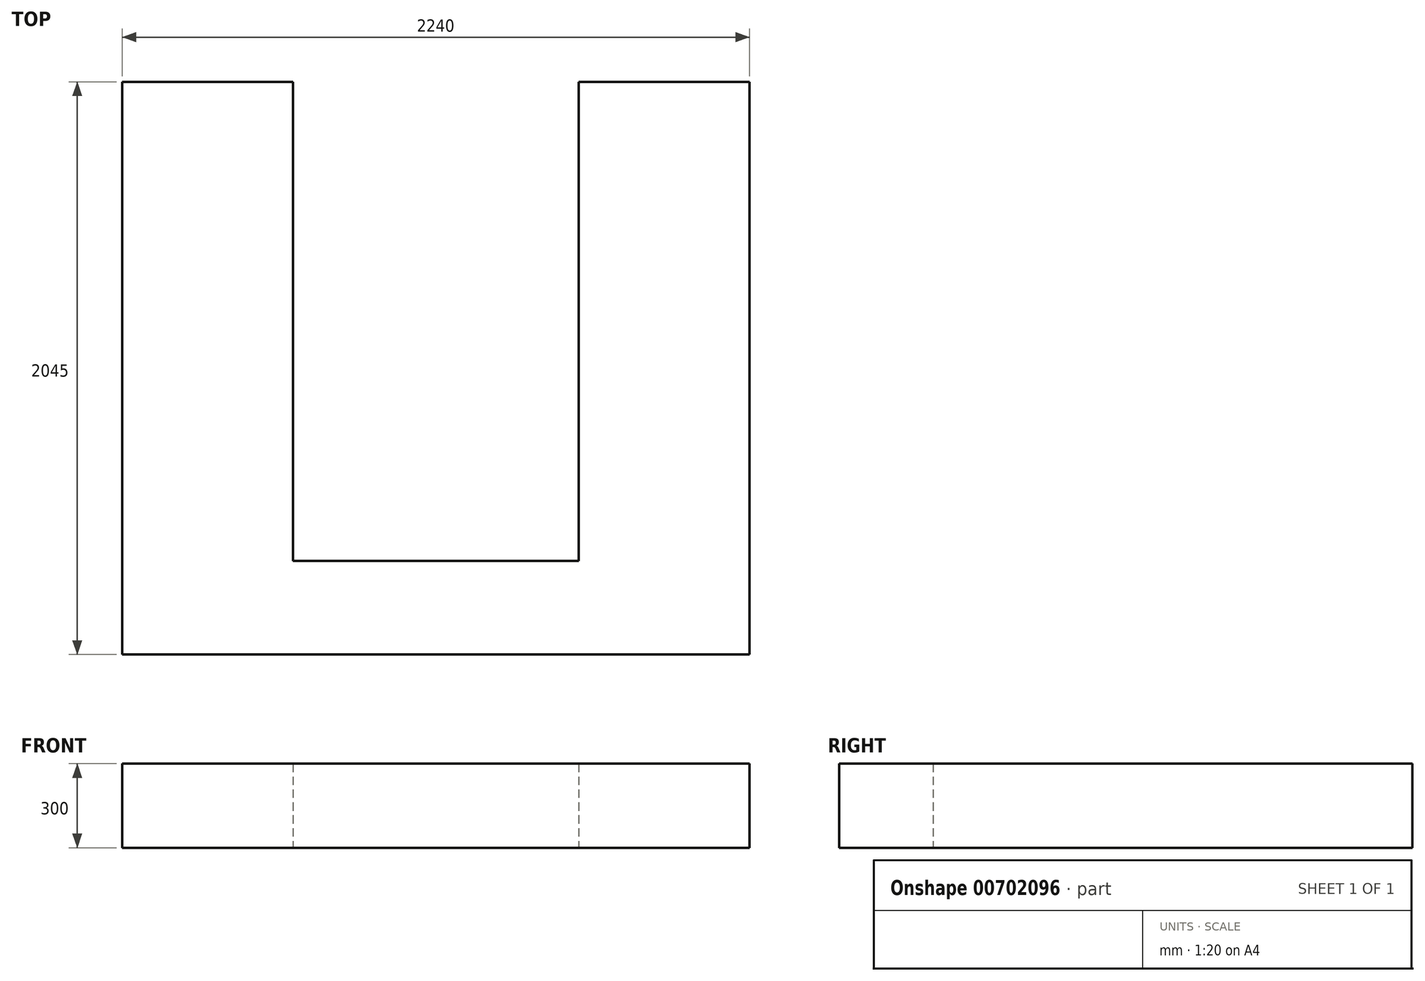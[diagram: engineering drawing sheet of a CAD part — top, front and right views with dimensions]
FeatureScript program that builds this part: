
annotation { "Feature Type Name" : "Feature", "Feature Type Description" : "" }
export const myFeature = defineFeature(function(context is Context, id is Id, definition is map)
    precondition{}
    {
        {
            var Q0;
            Q0=qCreatedBy(makeId("Top.planeOp"),FACE);
            var sketch = newSketch(context, id + "F0", { "sketchPlane" : qUnion([Q0])});
            skLineSegment(sketch, "E0", {"start": v(0, 0) * mm, "end": v(2240, 0) * mm});
            skLineSegment(sketch, "E1", {"start": v(2240, 0) * mm, "end": v(2240, 2045) * mm});
            skLineSegment(sketch, "E2", {"start": v(2240, 2045) * mm, "end": v(1630, 2045) * mm});
            skLineSegment(sketch, "E3", {"start": v(1630, 2045) * mm, "end": v(1630, 335) * mm});
            skLineSegment(sketch, "E4", {"start": v(1630, 335) * mm, "end": v(610, 335) * mm});
            skLineSegment(sketch, "E5", {"start": v(610, 335) * mm, "end": v(610, 2045) * mm});
            skLineSegment(sketch, "E6", {"start": v(610, 2045) * mm, "end": v(0, 2045) * mm});
            skLineSegment(sketch, "E7", {"start": v(0, 2045) * mm, "end": v(0, 0) * mm});
            skSolve(sketch);
        }
        {
            var Q0;
            Q0=makeQuery(id+"F0.imprint","IMPRINT",FACE,{"disambiguationData":[TD([[makeQuery(id+"F0.imprint","IMPRINT",EDGE,{"derivedFrom":sQuery(id+"F0.wireOp",EDGE,"E0")}),1.0]])]});
            extrude(context, id + "F1", {"entities" : qUnion([Q0]), "depth" : 300 * mm, "offsetDistance" : 25 * mm});
        }
    });
